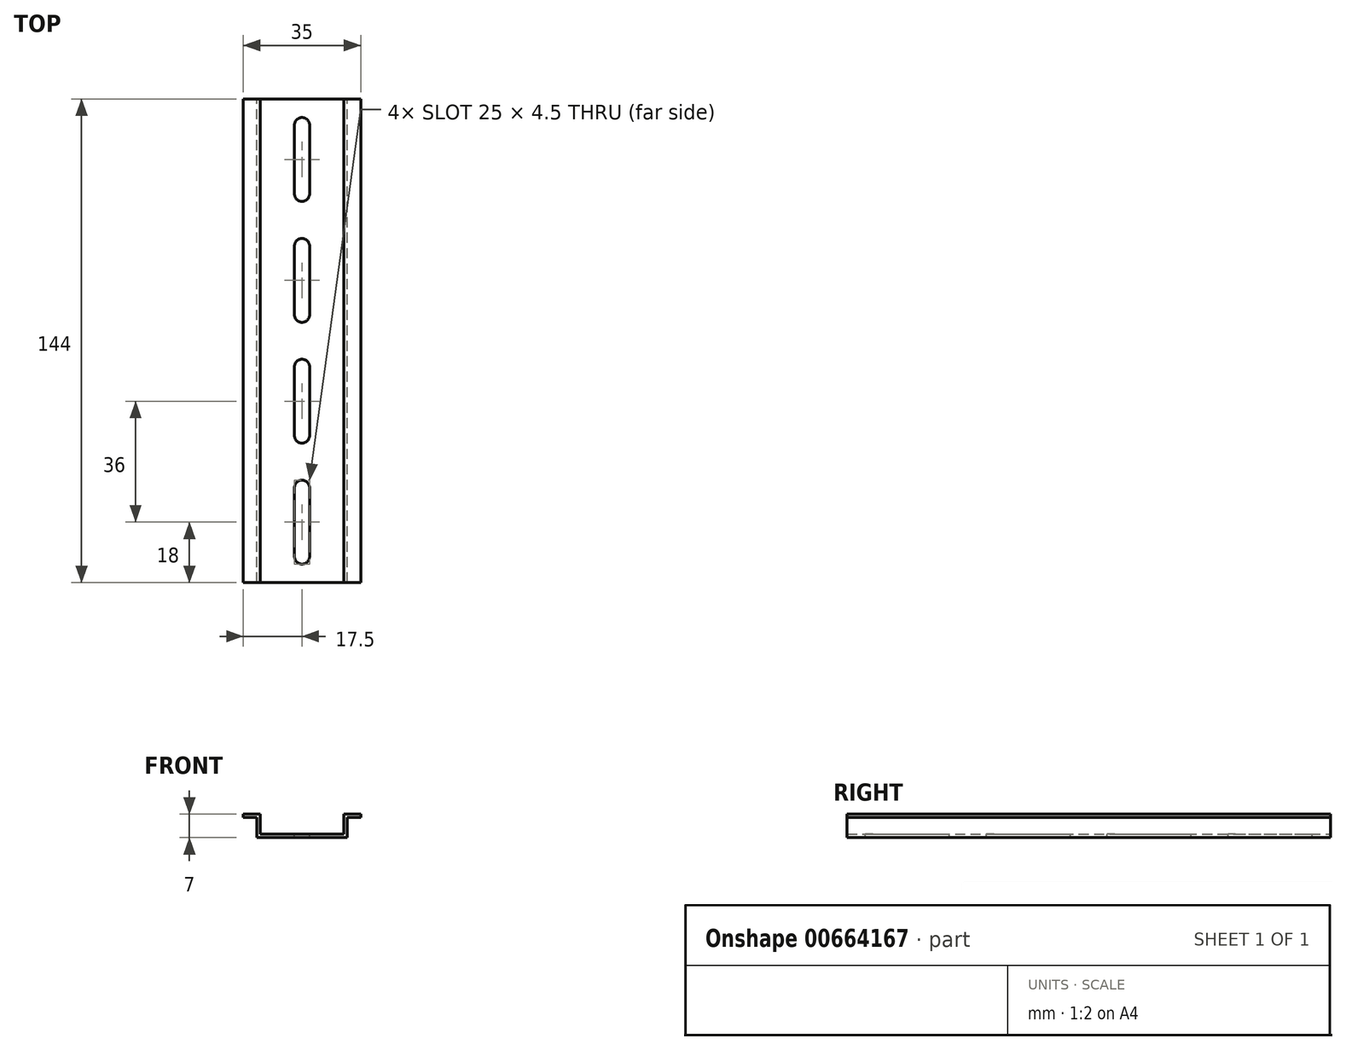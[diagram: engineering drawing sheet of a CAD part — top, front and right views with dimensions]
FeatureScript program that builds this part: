
annotation { "Feature Type Name" : "Feature", "Feature Type Description" : "" }
export const myFeature = defineFeature(function(context is Context, id is Id, definition is map)
    precondition{}
    {
        {
            var Q0;
            Q0=qCreatedBy(makeId("Front.planeOp"),FACE);
            var sketch = newSketch(context, id + "F0", { "sketchPlane" : qUnion([Q0])});
            skLineSegment(sketch, "E0", {"start": v(-17.5, 5) * mm, "end": v(-13.5, 5) * mm});
            skLineSegment(sketch, "E1", {"start": v(-13.5, 5) * mm, "end": v(-13.5, -1) * mm});
            skLineSegment(sketch, "E2", {"start": v(-13.5, -1) * mm, "end": v(13.5, -1) * mm});
            skLineSegment(sketch, "E3", {"start": v(13.5, -1) * mm, "end": v(13.5, 5) * mm});
            skLineSegment(sketch, "E4", {"start": v(13.5, 5) * mm, "end": v(17.5, 5) * mm});
            skLineSegment(sketch, "E5", {"start": v(17.5, 5) * mm, "end": v(17.5, 6) * mm});
            skLineSegment(sketch, "E6", {"start": v(17.5, 6) * mm, "end": v(12.5, 6) * mm});
            skLineSegment(sketch, "E7", {"start": v(12.5, 6) * mm, "end": v(12.5, 0) * mm});
            skLineSegment(sketch, "E8", {"start": v(12.5, 0) * mm, "end": v(-12.5, 0) * mm});
            skLineSegment(sketch, "E9", {"start": v(-12.5, 0) * mm, "end": v(-12.5, 6) * mm});
            skLineSegment(sketch, "E10", {"start": v(-12.5, 6) * mm, "end": v(-17.5, 6) * mm});
            skLineSegment(sketch, "E11", {"start": v(-17.5, 6) * mm, "end": v(-17.5, 5) * mm});
            skSolve(sketch);
        }
        {
            var Q0;
            Q0=makeQuery(id+"F0.imprint","IMPRINT",FACE,{"disambiguationData":[TD([[makeQuery(id+"F0.imprint","IMPRINT",EDGE,{"derivedFrom":sQuery(id+"F0.wireOp",EDGE,"E0")}),1.0]])]});
            extrude(context, id + "F1", {"entities" : qUnion([Q0]), "depth" : 144 * mm, "offsetDistance" : 25 * mm});
        }
        {
            var Q0;
            Q0=makeQuery(id+"F1.opExtrude","SWEPT_FACE",FACE,{"disambiguationData":[OSD([sQuery(id+"F0.wireOp",EDGE,"E8")])]});
            var sketch = newSketch(context, id + "F2", { "sketchPlane" : qUnion([Q0])});
            skLineSegment(sketch, "E12", {"start": v(0, 0) * mm, "end": v(0, -144) * mm, "construction": true});
            skLineSegment(sketch, "E13.left", {"start": v(2.25, -28.25) * mm, "end": v(2.25, -7.75) * mm});
            skLineSegment(sketch, "E13.right", {"start": v(-2.25, -28.25) * mm, "end": v(-2.25, -7.75) * mm});
            skPoint(sketch, "E13.middle", {"position": v(0, -18) * mm});
            skArc(sketch, "E14", {"start": v(2.25, -7.75) * mm, "mid": v(0, -5.5) * mm, "end": v(-2.25, -7.75) * mm});
            skArc(sketch, "E15", {"start": v(2.25, -28.25) * mm, "mid": v(0, -30.5) * mm, "end": v(-2.25, -28.25) * mm});
            skLineSegment(sketch, "E16.0.1.0", {"start": v(-2.25, -64.25) * mm, "end": v(-2.25, -43.75) * mm});
            skArc(sketch, "E16.0.1.1", {"start": v(2.25, -43.75) * mm, "mid": v(0, -41.5) * mm, "end": v(-2.25, -43.75) * mm});
            skLineSegment(sketch, "E16.0.1.2", {"start": v(2.25, -64.25) * mm, "end": v(2.25, -43.75) * mm});
            skPoint(sketch, "E16.0.1.3", {"position": v(0, -54) * mm});
            skArc(sketch, "E16.0.1.4", {"start": v(2.25, -64.25) * mm, "mid": v(0, -66.5) * mm, "end": v(-2.25, -64.25) * mm});
            skLineSegment(sketch, "E16.0.2.0", {"start": v(-2.25, -100.25) * mm, "end": v(-2.25, -79.75) * mm});
            skArc(sketch, "E16.0.2.1", {"start": v(2.25, -79.75) * mm, "mid": v(0, -77.5) * mm, "end": v(-2.25, -79.75) * mm});
            skLineSegment(sketch, "E16.0.2.2", {"start": v(2.25, -100.25) * mm, "end": v(2.25, -79.75) * mm});
            skPoint(sketch, "E16.0.2.3", {"position": v(0, -90) * mm});
            skArc(sketch, "E16.0.2.4", {"start": v(2.25, -100.25) * mm, "mid": v(0, -102.5) * mm, "end": v(-2.25, -100.25) * mm});
            skLineSegment(sketch, "E16.0.3.0", {"start": v(-2.25, -136.25) * mm, "end": v(-2.25, -115.75) * mm});
            skArc(sketch, "E16.0.3.1", {"start": v(2.25, -115.75) * mm, "mid": v(0, -113.5) * mm, "end": v(-2.25, -115.75) * mm});
            skLineSegment(sketch, "E16.0.3.2", {"start": v(2.25, -136.25) * mm, "end": v(2.25, -115.75) * mm});
            skPoint(sketch, "E16.0.3.3", {"position": v(0, -126) * mm});
            skArc(sketch, "E16.0.3.4", {"start": v(2.25, -136.25) * mm, "mid": v(0, -138.5) * mm, "end": v(-2.25, -136.25) * mm});
            skLineSegment(sketch, "E16.0.4.0", {"start": v(-2.25, -172.25) * mm, "end": v(-2.25, -151.75) * mm});
            skArc(sketch, "E16.0.4.1", {"start": v(2.25, -151.75) * mm, "mid": v(0, -149.5) * mm, "end": v(-2.25, -151.75) * mm});
            skLineSegment(sketch, "E16.0.4.2", {"start": v(2.25, -172.25) * mm, "end": v(2.25, -151.75) * mm});
            skPoint(sketch, "E16.0.4.3", {"position": v(0, -162) * mm});
            skArc(sketch, "E16.0.4.4", {"start": v(2.25, -172.25) * mm, "mid": v(0, -174.5) * mm, "end": v(-2.25, -172.25) * mm});
            skLineSegment(sketch, "E16.direction1", {"start": v(-2.25, -28.25) * mm, "end": v(22.75, -28.25) * mm, "construction": true});
            skLineSegment(sketch, "E16.direction2", {"start": v(-2.25, -28.25) * mm, "end": v(-2.25, -64.25) * mm, "construction": true});
            skSolve(sketch);
        }
        {
            var Q0;
            Q0=makeQuery(id+"F2.imprint","IMPRINT",FACE,{"disambiguationData":[TD([[makeQuery(id+"F2.imprint","IMPRINT",EDGE,{"derivedFrom":sQuery(id+"F2.wireOp",EDGE,"E13.left")}),1.0]])]});
            var Q1;
            Q1=makeQuery(id+"F2.imprint","IMPRINT",FACE,{"disambiguationData":[TD([[makeQuery(id+"F2.imprint","IMPRINT",EDGE,{"derivedFrom":sQuery(id+"F2.wireOp",EDGE,"E16.0.1.0")}),-1.0]])]});
            var Q2;
            Q2=makeQuery(id+"F2.imprint","IMPRINT",FACE,{"disambiguationData":[TD([[makeQuery(id+"F2.imprint","IMPRINT",EDGE,{"derivedFrom":sQuery(id+"F2.wireOp",EDGE,"E16.0.2.0")}),-1.0]])]});
            var Q3;
            Q3=makeQuery(id+"F2.imprint","IMPRINT",FACE,{"disambiguationData":[TD([[makeQuery(id+"F2.imprint","IMPRINT",EDGE,{"derivedFrom":sQuery(id+"F2.wireOp",EDGE,"E16.0.3.0")}),-1.0]])]});
            var Q4;
            {var subQ0=sQuery(id+"F2.wireOp",EDGE,"E16.0.4.1");var subQ1=makeQuery(id+"F1.opExtrude","CAP_EDGE",EDGE,{"disambiguationData":[OSD([sQuery(id+"F0.wireOp",EDGE,"E8")])],"isStart":false});var subQ2=makeQuery(id+"F2.imprint","INTERSECT",VERTEX,{"disambiguationData":[OD(0.0)],"derivedFrom":[subQ1,subQ0]});Q4=makeQuery(id+"F2.imprint","IMPRINT",FACE,{"disambiguationData":[TD([[makeQuery(id+"F2.imprint","IMPRINT",EDGE,{"disambiguationData":[TD([[subQ2,-1.0]])],"derivedFrom":subQ0}),1.0]])]});}
            extrude(context, id + "F3", {"entities" : qUnion([Q0, Q1, Q2, Q3, Q4]), "operationType" : NewBodyOperationType.REMOVE, "endBound" : BoundingType.THROUGH_ALL, "oppositeDirection" : true, "depth" : 25 * mm, "offsetDistance" : 25 * mm});
        }
    });
